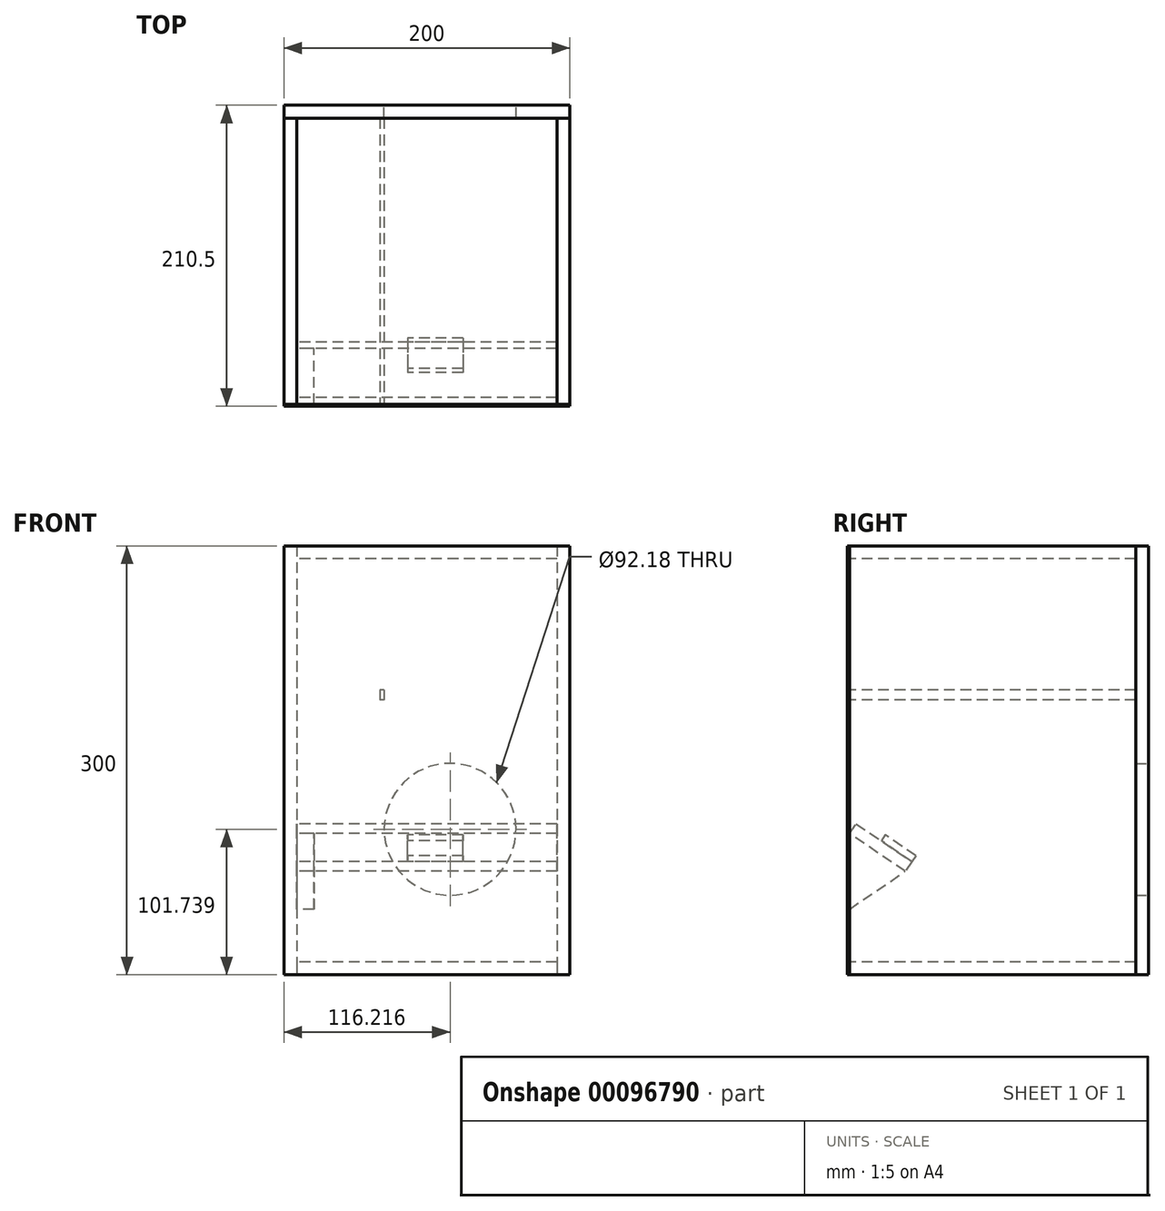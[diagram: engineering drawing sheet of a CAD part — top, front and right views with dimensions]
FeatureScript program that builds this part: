
annotation { "Feature Type Name" : "Feature", "Feature Type Description" : "" }
export const myFeature = defineFeature(function(context is Context, id is Id, definition is map)
    precondition{}
    {
        {
            var Q0;
            Q0=qCreatedBy(makeId("Front.planeOp"),FACE);
            var sketch = newSketch(context, id + "F0", { "sketchPlane" : qUnion([Q0])});
            skLineSegment(sketch, "E0.bottom", {"start": v(0, 0) * mm, "end": v(200, 0) * mm});
            skLineSegment(sketch, "E0.top", {"start": v(0, 300) * mm, "end": v(200, 300) * mm});
            skLineSegment(sketch, "E0.left", {"start": v(0, 0) * mm, "end": v(0, 300) * mm});
            skLineSegment(sketch, "E0.right", {"start": v(200, 0) * mm, "end": v(200, 300) * mm});
            skSolve(sketch);
        }
        {
            var Q0;
            Q0 = qSketchRegion(id + "F0", true);
            extrude(context, id + "F1", {"entities" : qUnion([Q0]), "depth" : 1.5 * mm});
        }
        {
            var Q0;
            Q0=makeQuery(id+"F1.opExtrude","CAP_FACE",FACE,{"disambiguationData":[OSD([sQuery(id+"F0.wireOp",EDGE,"E0.bottom"),sQuery(id+"F0.wireOp",EDGE,"E0.top"),sQuery(id+"F0.wireOp",EDGE,"E0.left"),sQuery(id+"F0.wireOp",EDGE,"E0.right")])],"isStart":true});
            var sketch = newSketch(context, id + "F2", { "sketchPlane" : qUnion([Q0])});
            skLineSegment(sketch, "E1.bottom", {"start": v(0, 300) * mm, "end": v(-9, 300) * mm});
            skLineSegment(sketch, "E1.top", {"start": v(0, 0) * mm, "end": v(-9, 0) * mm});
            skLineSegment(sketch, "E1.left", {"start": v(0, 300) * mm, "end": v(0, 0) * mm});
            skLineSegment(sketch, "E1.right", {"start": v(-9, 300) * mm, "end": v(-9, 0) * mm});
            skLineSegment(sketch, "E2.bottom", {"start": v(-69.99, 199.06) * mm, "end": v(-67.2, 199.06) * mm});
            skLineSegment(sketch, "E2.top", {"start": v(-69.99, 192.11) * mm, "end": v(-67.2, 192.11) * mm});
            skLineSegment(sketch, "E2.left", {"start": v(-69.99, 199.06) * mm, "end": v(-69.99, 192.11) * mm});
            skLineSegment(sketch, "E2.right", {"start": v(-67.2, 199.06) * mm, "end": v(-67.2, 192.11) * mm});
            skSolve(sketch);
        }
        {
            var Q0;
            Q0 = qSketchRegion(id + "F2", true);
            extrude(context, id + "F3", {"entities" : qUnion([Q0]), "depth" : 200 * mm});
        }
        {
            var Q0;
            Q0=makeQuery(id+"F3.opExtrude","SWEPT_FACE",FACE,{"disambiguationData":[OSD([sQuery(id+"F2.wireOp",EDGE,"E1.right")])]});
            var sketch = newSketch(context, id + "F4", { "sketchPlane" : qUnion([Q0])});
            skLineSegment(sketch, "E3", {"start": v(0, 98.82) * mm, "end": v(0, 45.95) * mm});
            skLineSegment(sketch, "E4", {"start": v(0, 45.95) * mm, "end": v(38.85, 72.38) * mm});
            skLineSegment(sketch, "E5", {"start": v(38.85, 72.38) * mm, "end": v(0, 98.82) * mm});
            skSolve(sketch);
        }
        {
            var Q0;
            Q0 = qSketchRegion(id + "F4", true);
            extrude(context, id + "F5", {"entities" : qUnion([Q0]), "depth" : 12 * mm});
        }
        {
            var Q0;
            Q0=makeQuery(id+"F3.opExtrude","SWEPT_FACE",FACE,{"disambiguationData":[OSD([sQuery(id+"F2.wireOp",EDGE,"E1.right")])]});
            var sketch = newSketch(context, id + "F6", { "sketchPlane" : qUnion([Q0])});
            skLineSegment(sketch, "E6", {"start": v(38.86, 72.38) * mm, "end": v(0, 98.8) * mm});
            skLineSegment(sketch, "E7", {"start": v(0, 98.8) * mm, "end": v(4.63, 105.6) * mm});
            skLineSegment(sketch, "E8", {"start": v(4.63, 105.6) * mm, "end": v(43.48, 79.19) * mm});
            skLineSegment(sketch, "E9", {"start": v(43.48, 79.19) * mm, "end": v(38.86, 72.38) * mm});
            skSolve(sketch);
        }
        {
            var Q0;
            Q0 = qSketchRegion(id + "F6", true);
            extrude(context, id + "F7", {"entities" : qUnion([Q0]), "depth" : 182 * mm});
        }
        {
            var Q0;
            Q0=makeQuery(id+"F7.opExtrude","SWEPT_FACE",FACE,{"disambiguationData":[OSD([sQuery(id+"F6.wireOp",EDGE,"E8")])]});
            var sketch = newSketch(context, id + "F8", { "sketchPlane" : qUnion([Q0])});
            skLineSegment(sketch, "E10.bottom", {"start": v(125.11, -8.56) * mm, "end": v(86.62, -8.56) * mm});
            skLineSegment(sketch, "E10.top", {"start": v(125.11, -34.4) * mm, "end": v(86.62, -34.4) * mm});
            skLineSegment(sketch, "E10.left", {"start": v(125.11, -8.56) * mm, "end": v(125.11, -34.4) * mm});
            skLineSegment(sketch, "E10.right", {"start": v(86.62, -8.56) * mm, "end": v(86.62, -34.4) * mm});
            skSolve(sketch);
        }
        {
            var Q0;
            Q0 = qSketchRegion(id + "F8", true);
            extrude(context, id + "F9", {"entities" : qUnion([Q0]), "depth" : 5 * mm});
        }
        {
            var Q0;
            Q0=makeQuery(id+"F3.opExtrude","SWEPT_FACE",FACE,{"disambiguationData":[OSD([sQuery(id+"F2.wireOp",EDGE,"E1.right")])]});
            var sketch = newSketch(context, id + "F10", { "sketchPlane" : qUnion([Q0])});
            skLineSegment(sketch, "E11.bottom", {"start": v(200, 300) * mm, "end": v(0, 300) * mm});
            skLineSegment(sketch, "E11.top", {"start": v(200, 291) * mm, "end": v(0, 291) * mm});
            skLineSegment(sketch, "E11.left", {"start": v(200, 300) * mm, "end": v(200, 291) * mm});
            skLineSegment(sketch, "E11.right", {"start": v(0, 300) * mm, "end": v(0, 291) * mm});
            skSolve(sketch);
        }
        {
            var Q0;
            Q0 = qSketchRegion(id + "F10", true);
            extrude(context, id + "F11", {"entities" : qUnion([Q0]), "depth" : 182 * mm});
        }
        {
            var Q0;
            Q0=makeQuery(id+"F3.opExtrude","SWEPT_FACE",FACE,{"disambiguationData":[OSD([sQuery(id+"F2.wireOp",EDGE,"E1.right")])]});
            var sketch = newSketch(context, id + "F12", { "sketchPlane" : qUnion([Q0])});
            skLineSegment(sketch, "E12.bottom", {"start": v(200, 0) * mm, "end": v(0, 0) * mm});
            skLineSegment(sketch, "E12.top", {"start": v(200, 9) * mm, "end": v(0, 9) * mm});
            skLineSegment(sketch, "E12.left", {"start": v(200, 0) * mm, "end": v(200, 9) * mm});
            skLineSegment(sketch, "E12.right", {"start": v(0, 0) * mm, "end": v(0, 9) * mm});
            skSolve(sketch);
        }
        {
            var Q0;
            Q0 = qSketchRegion(id + "F12", true);
            extrude(context, id + "F13", {"entities" : qUnion([Q0]), "depth" : 182 * mm});
        }
        {
            var Q0;
            Q0=makeQuery(id+"F11.opExtrude","CAP_FACE",FACE,{"disambiguationData":[OSD([sQuery(id+"F10.wireOp",EDGE,"E11.bottom"),sQuery(id+"F10.wireOp",EDGE,"E11.top"),sQuery(id+"F10.wireOp",EDGE,"E11.left"),sQuery(id+"F10.wireOp",EDGE,"E11.right")])],"isStart":false});
            var sketch = newSketch(context, id + "F14", { "sketchPlane" : qUnion([Q0])});
            skLineSegment(sketch, "E13.bottom", {"start": v(200, 300) * mm, "end": v(0, 300) * mm});
            skLineSegment(sketch, "E13.top", {"start": v(200, 0) * mm, "end": v(0, 0) * mm});
            skLineSegment(sketch, "E13.left", {"start": v(200, 300) * mm, "end": v(200, 0) * mm});
            skLineSegment(sketch, "E13.right", {"start": v(0, 300) * mm, "end": v(0, 0) * mm});
            skSolve(sketch);
        }
        {
            var Q0;
            Q0 = qSketchRegion(id + "F14", true);
            extrude(context, id + "F15", {"entities" : qUnion([Q0]), "depth" : 9 * mm});
        }
        {
            var Q0;
            Q0=makeQuery(id+"F15.opExtrude","SWEPT_FACE",FACE,{"disambiguationData":[OSD([sQuery(id+"F14.wireOp",EDGE,"E13.left")])]});
            var sketch = newSketch(context, id + "F16", { "sketchPlane" : qUnion([Q0])});
            skLineSegment(sketch, "E14.bottom", {"start": v(-200, 300) * mm, "end": v(0, 300) * mm});
            skLineSegment(sketch, "E14.top", {"start": v(-200, 0) * mm, "end": v(0, 0) * mm});
            skLineSegment(sketch, "E14.left", {"start": v(-200, 300) * mm, "end": v(-200, 0) * mm});
            skLineSegment(sketch, "E14.right", {"start": v(0, 300) * mm, "end": v(0, 0) * mm});
            skSolve(sketch);
        }
        {
            var Q0;
            Q0 = qSketchRegion(id + "F16", true);
            extrude(context, id + "F17", {"entities" : qUnion([Q0]), "depth" : 9 * mm});
        }
        {
            var Q0;
            Q0=makeQuery(id+"F17.opExtrude","CAP_FACE",FACE,{"disambiguationData":[OSD([sQuery(id+"F16.wireOp",EDGE,"E14.bottom"),sQuery(id+"F16.wireOp",EDGE,"E14.top"),sQuery(id+"F16.wireOp",EDGE,"E14.left"),sQuery(id+"F16.wireOp",EDGE,"E14.right")])],"isStart":false});
            var sketch = newSketch(context, id + "F18", { "sketchPlane" : qUnion([Q0])});
            skCircle(sketch, "E15", {"center": v(-116.22, 101.74) * mm, "radius": 46.1 * mm});
            skSolve(sketch);
        }
        {
            var Q0;
            Q0 = qSketchRegion(id + "F18", true);
            extrude(context, id + "F19", {"entities" : qUnion([Q0]), "operationType" : NewBodyOperationType.REMOVE, "oppositeDirection" : true, "depth" : 9 * mm});
        }
    });
